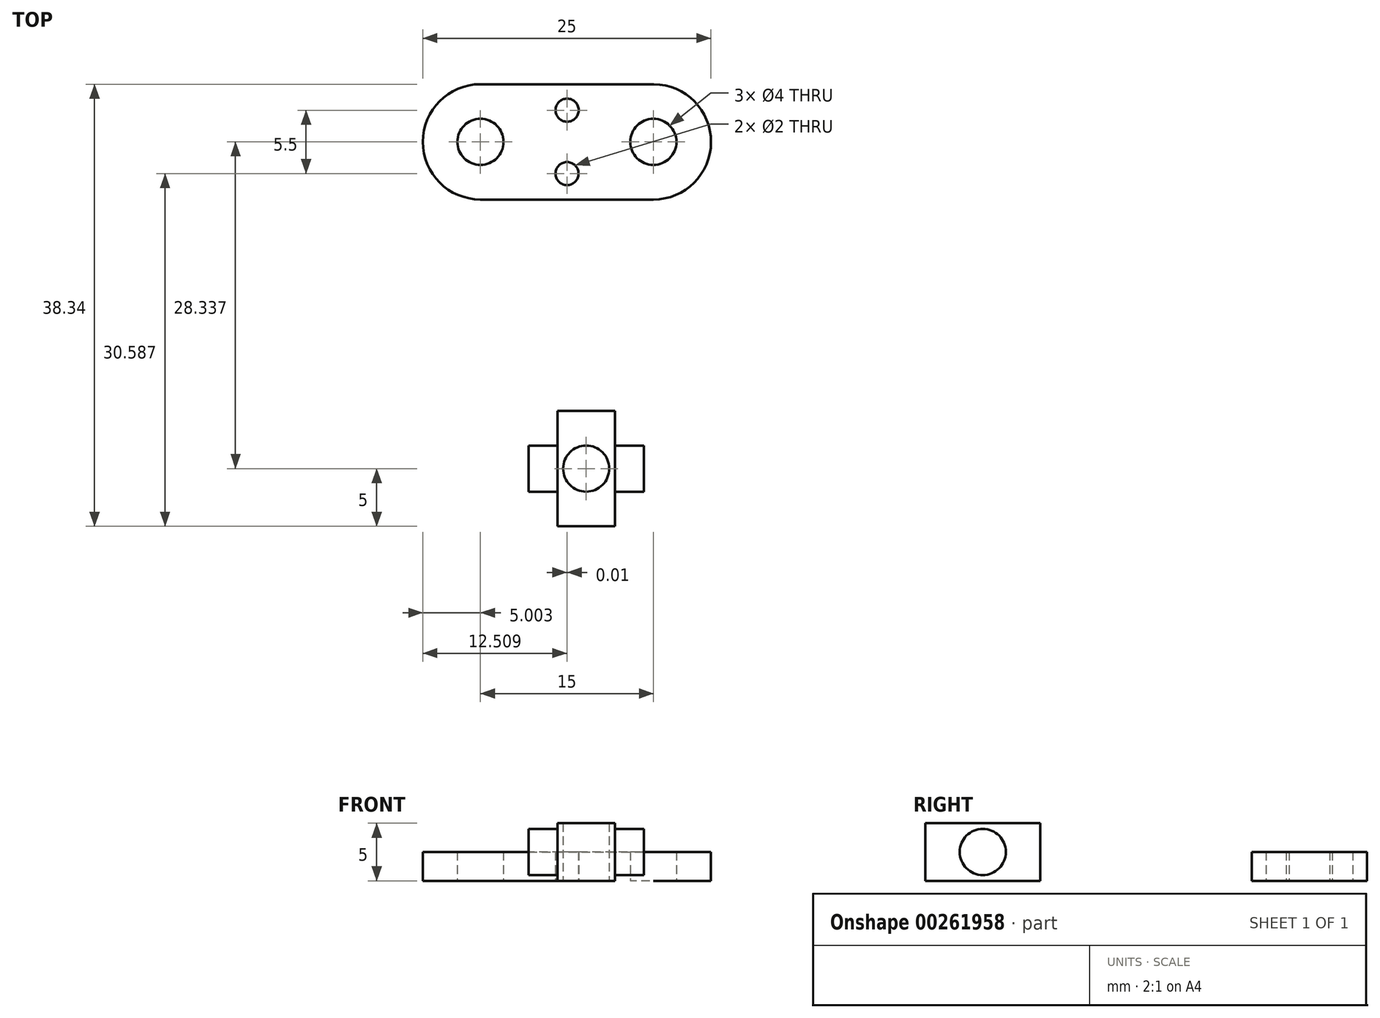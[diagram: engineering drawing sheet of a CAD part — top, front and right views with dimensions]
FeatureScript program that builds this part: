
annotation { "Feature Type Name" : "Feature", "Feature Type Description" : "" }
export const myFeature = defineFeature(function(context is Context, id is Id, definition is map)
    precondition{}
    {
        {
            var Q0;
            Q0=qCreatedBy(makeId("Top.planeOp"),FACE);
            var sketch = newSketch(context, id + "F0", { "sketchPlane" : qUnion([Q0])});
            skCircle(sketch, "E0", {"center": v(-61.88, 45.9) * mm, "radius": 5 * mm});
            skCircle(sketch, "E1", {"center": v(-61.88, 45.9) * mm, "radius": 2 * mm});
            skArc(sketch, "E2", {"start": v(-9.62, 50.9) * mm, "mid": v(-14.62, 45.9) * mm, "end": v(-9.62, 40.9) * mm});
            skArc(sketch, "E3", {"start": v(5.38, 40.9) * mm, "mid": v(10.38, 45.93) * mm, "end": v(5.34, 50.9) * mm});
            skLineSegment(sketch, "E4", {"start": v(5.43, 50.9) * mm, "end": v(-9.62, 50.9) * mm});
            skLineSegment(sketch, "E5", {"start": v(-9.62, 40.9) * mm, "end": v(5.38, 40.9) * mm});
            skCircle(sketch, "E6", {"center": v(-9.62, 45.9) * mm, "radius": 2 * mm});
            skCircle(sketch, "E7", {"center": v(5.38, 45.9) * mm, "radius": 2 * mm});
            skLineSegment(sketch, "E8.bottom", {"start": v(-9.62, 50.9) * mm, "end": v(5.41, 50.9) * mm});
            skLineSegment(sketch, "E8.top", {"start": v(-9.62, 47.9) * mm, "end": v(-2.76, 47.9) * mm});
            skLineSegment(sketch, "E9", {"start": v(-9.62, 43.9) * mm, "end": v(-2.77, 43.9) * mm});
            skCircle(sketch, "E10", {"center": v(-2.1, 48.66) * mm, "radius": 1 * mm});
            skCircle(sketch, "E11", {"center": v(-2.11, 43.16) * mm, "radius": 1 * mm});
            skLineSegment(sketch, "E12.trimOffspring", {"start": v(-1.45, 43.9) * mm, "end": v(5.4, 43.9) * mm});
            skLineSegment(sketch, "E13.trimOffspring", {"start": v(-1.44, 47.9) * mm, "end": v(5.41, 47.9) * mm});
            skPoint(sketch, "E14.trimOffspring.end.orphan", {"position": v(-2.1, 50.9) * mm});
            skSolve(sketch);
        }
        {
            var Q0;
            {var subQ15=sQuery(id+"F0.wireOp",EDGE,"E2");Q0=makeQuery(id+"F0.imprint","IMPRINT",FACE,{"disambiguationData":[TD([[makeQuery(id+"F0.imprint","IMPRINT",EDGE,{"derivedFrom":subQ15}),1.0]])]});}
            var Q1;
            {var subQ0=sQuery(id+"F0.wireOp",EDGE,"E9");Q1=makeQuery(id+"F0.imprint","IMPRINT",FACE,{"disambiguationData":[TD([[makeQuery(id+"F0.imprint","IMPRINT",EDGE,{"derivedFrom":subQ0}),1.0]])]});}
            extrude(context, id + "F1", {"entities" : qUnion([Q0, Q1]), "depth" : 2.5 * mm});
        }
        {
            var Q0;
            Q0=qCreatedBy(makeId("Top.planeOp"),FACE);
            var sketch = newSketch(context, id + "F2", { "sketchPlane" : qUnion([Q0])});
            skLineSegment(sketch, "E15.bottom", {"start": v(-2.95, 22.57) * mm, "end": v(2.05, 22.57) * mm});
            skLineSegment(sketch, "E15.top", {"start": v(-2.95, 12.57) * mm, "end": v(2.05, 12.57) * mm});
            skLineSegment(sketch, "E15.left", {"start": v(-2.95, 22.57) * mm, "end": v(-2.95, 12.57) * mm});
            skLineSegment(sketch, "E15.right", {"start": v(2.05, 22.57) * mm, "end": v(2.05, 12.57) * mm});
            skCircle(sketch, "E16", {"center": v(-0.45, 17.57) * mm, "radius": 2 * mm});
            skPoint(sketch, "E16.centerSnap0", {"position": v(-0.45, 22.57) * mm});
            skPoint(sketch, "E16.centerSnap1", {"position": v(-2.95, 17.57) * mm});
            skLineSegment(sketch, "E17.bottom", {"start": v(1.11, 16.32) * mm, "end": v(-2, 16.32) * mm});
            skLineSegment(sketch, "E17.top", {"start": v(1.11, 18.82) * mm, "end": v(-2, 18.82) * mm});
            skSolve(sketch);
        }
        {
            var Q0;
            Q0 = qSketchRegion(id + "F2", true);
            extrude(context, id + "F3", {"entities" : qUnion([Q0]), "depth" : 5 * mm});
        }
        {
            var Q0;
            Q0=makeQuery(id+"F3.opExtrude","SWEPT_FACE",FACE,{"disambiguationData":[OSD([sQuery(id+"F2.wireOp",EDGE,"E15.right")])]});
            var sketch = newSketch(context, id + "F4", { "sketchPlane" : qUnion([Q0])});
            skCircle(sketch, "E18", {"center": v(17.57, 2.5) * mm, "radius": 2 * mm});
            skPoint(sketch, "E18.centerSnap0", {"position": v(17.57, 5) * mm});
            skPoint(sketch, "E18.centerSnap1", {"position": v(22.57, 2.5) * mm});
            skSolve(sketch);
        }
        {
            var Q0;
            Q0 = qSketchRegion(id + "F4", true);
            extrude(context, id + "F5", {"entities" : qUnion([Q0]), "operationType" : NewBodyOperationType.ADD, "depth" : 2.5 * mm});
        }
        {
            var Q0;
            Q0=makeQuery(id+"F3.opExtrude","SWEPT_FACE",FACE,{"disambiguationData":[OSD([sQuery(id+"F2.wireOp",EDGE,"E15.left")])]});
            var sketch = newSketch(context, id + "F6", { "sketchPlane" : qUnion([Q0])});
            skCircle(sketch, "E19", {"center": v(-17.57, 2.5) * mm, "radius": 2 * mm});
            skPoint(sketch, "E19.centerSnap0", {"position": v(-17.57, 5) * mm});
            skPoint(sketch, "E19.centerSnap1", {"position": v(-22.57, 2.5) * mm});
            skSolve(sketch);
        }
        {
            var Q0;
            Q0 = qSketchRegion(id + "F6", true);
            extrude(context, id + "F7", {"entities" : qUnion([Q0]), "operationType" : NewBodyOperationType.ADD, "depth" : 2.5 * mm});
        }
    });
